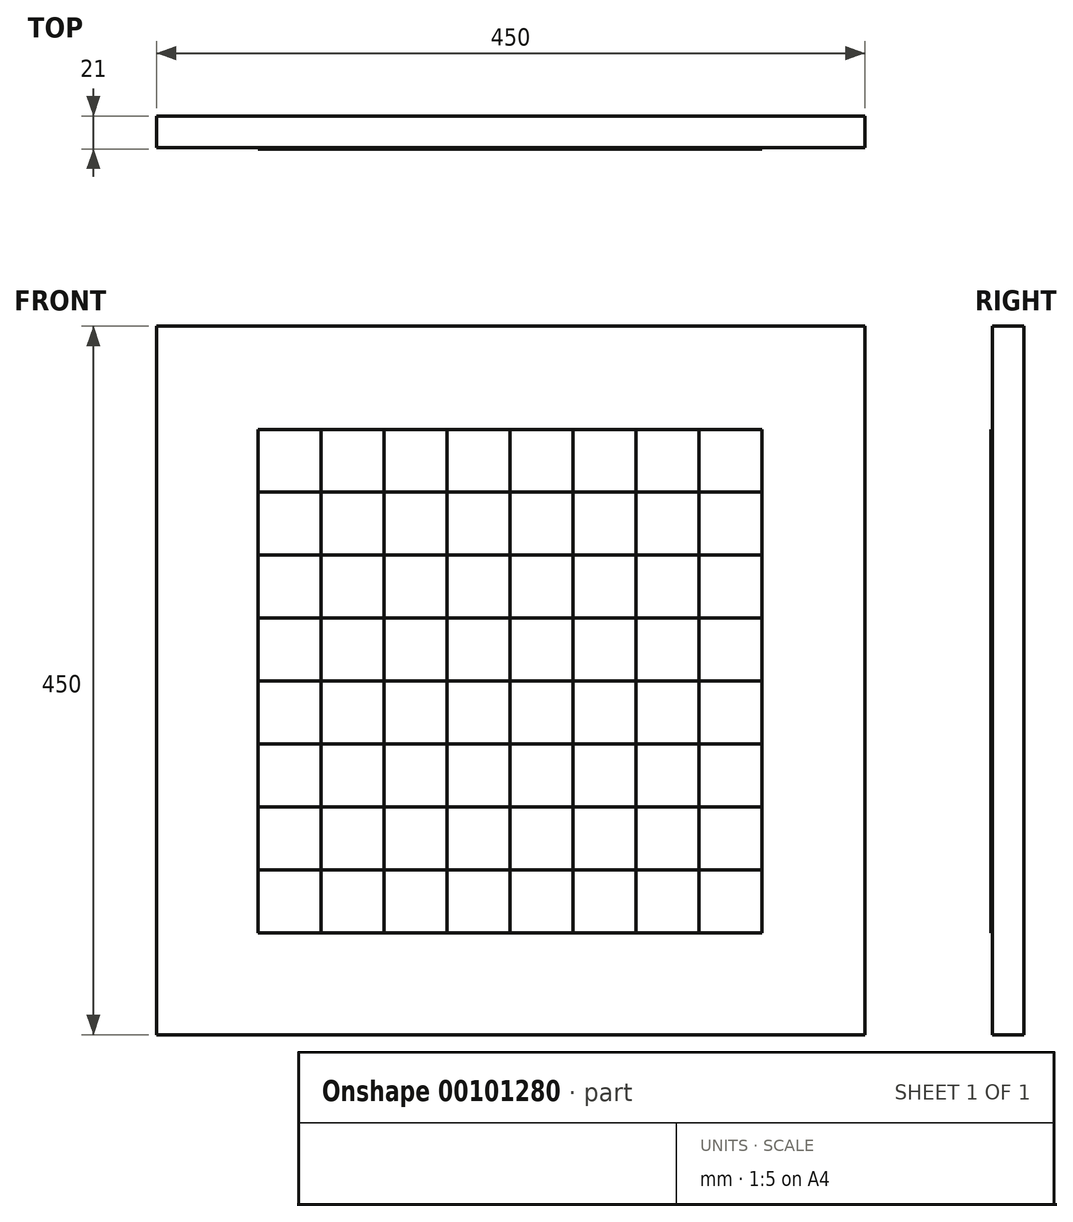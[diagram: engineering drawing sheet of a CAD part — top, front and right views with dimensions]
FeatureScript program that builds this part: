
annotation { "Feature Type Name" : "Feature", "Feature Type Description" : "" }
export const myFeature = defineFeature(function(context is Context, id is Id, definition is map)
    precondition{}
    {
        {
            var Q0;
            Q0=qCreatedBy(makeId("Front.planeOp"),FACE);
            var sketch = newSketch(context, id + "F0", { "sketchPlane" : qUnion([Q0])});
            skLineSegment(sketch, "E0.bottom", {"start": v(0, 0) * mm, "end": v(-450, 0) * mm});
            skLineSegment(sketch, "E0.top", {"start": v(0, 450) * mm, "end": v(-450, 450) * mm});
            skLineSegment(sketch, "E0.left", {"start": v(0, 0) * mm, "end": v(0, 450) * mm});
            skLineSegment(sketch, "E0.right", {"start": v(-450, 0) * mm, "end": v(-450, 450) * mm});
            skSolve(sketch);
        }
        {
            var Q0;
            Q0=makeQuery(id+"F0.imprint","IMPRINT",FACE,{"disambiguationData":[TD([[makeQuery(id+"F0.imprint","IMPRINT",EDGE,{"derivedFrom":sQuery(id+"F0.wireOp",EDGE,"E0.bottom")}),-1.0]])]});
            extrude(context, id + "F1", {"entities" : qUnion([Q0]), "depth" : 20 * mm});
        }
        {
            var Q0;
            Q0=makeQuery(id+"F1.opExtrude","CAP_FACE",FACE,{"disambiguationData":[OSD([sQuery(id+"F0.wireOp",EDGE,"E0.bottom"),sQuery(id+"F0.wireOp",EDGE,"E0.top"),sQuery(id+"F0.wireOp",EDGE,"E0.left"),sQuery(id+"F0.wireOp",EDGE,"E0.right")])],"isStart":false});
            var sketch = newSketch(context, id + "F2", { "sketchPlane" : qUnion([Q0])});
            skLineSegment(sketch, "E1.bottom", {"start": v(-65.47, 64.53) * mm, "end": v(-385.47, 64.53) * mm});
            skLineSegment(sketch, "E1.left", {"start": v(-65.47, 64.53) * mm, "end": v(-65.47, 384.53) * mm});
            skPoint(sketch, "E1.middle", {"position": v(-225.47, 224.53) * mm});
            skLineSegment(sketch, "E2", {"start": v(-65.47, 64.53) * mm, "end": v(0, 0) * mm});
            skLineSegment(sketch, "E3", {"start": v(-385.47, 384.53) * mm, "end": v(-345.47, 384.53) * mm});
            skLineSegment(sketch, "E4", {"start": v(-345.47, 384.53) * mm, "end": v(-305.47, 384.53) * mm});
            skLineSegment(sketch, "E5", {"start": v(-305.47, 384.53) * mm, "end": v(-265.47, 384.53) * mm});
            skLineSegment(sketch, "E6", {"start": v(-265.47, 384.53) * mm, "end": v(-225.47, 384.53) * mm});
            skLineSegment(sketch, "E7", {"start": v(-225.47, 384.53) * mm, "end": v(-185.47, 384.53) * mm});
            skLineSegment(sketch, "E8", {"start": v(-185.47, 384.53) * mm, "end": v(-145.47, 384.53) * mm});
            skLineSegment(sketch, "E9", {"start": v(-145.47, 384.53) * mm, "end": v(-105.47, 384.53) * mm});
            skLineSegment(sketch, "E10", {"start": v(-105.47, 384.53) * mm, "end": v(-65.47, 384.53) * mm});
            skLineSegment(sketch, "E11", {"start": v(-385.47, 384.53) * mm, "end": v(-385.47, 344.53) * mm});
            skLineSegment(sketch, "E12", {"start": v(-385.47, 344.53) * mm, "end": v(-385.47, 304.53) * mm});
            skLineSegment(sketch, "E13", {"start": v(-385.47, 304.53) * mm, "end": v(-385.47, 264.53) * mm});
            skLineSegment(sketch, "E14", {"start": v(-385.47, 264.53) * mm, "end": v(-385.47, 224.53) * mm});
            skLineSegment(sketch, "E15", {"start": v(-385.47, 224.53) * mm, "end": v(-385.47, 184.53) * mm});
            skLineSegment(sketch, "E16", {"start": v(-385.47, 184.53) * mm, "end": v(-385.47, 144.53) * mm});
            skLineSegment(sketch, "E17", {"start": v(-385.47, 144.53) * mm, "end": v(-385.47, 104.53) * mm});
            skLineSegment(sketch, "E18", {"start": v(-385.47, 104.53) * mm, "end": v(-385.47, 64.53) * mm});
            skLineSegment(sketch, "E19", {"start": v(-385.47, 344.53) * mm, "end": v(-65.47, 344.53) * mm});
            skLineSegment(sketch, "E20", {"start": v(-345.47, 384.53) * mm, "end": v(-345.47, 64.53) * mm});
            skLineSegment(sketch, "E21", {"start": v(-385.47, 304.53) * mm, "end": v(-65.47, 304.53) * mm});
            skLineSegment(sketch, "E22", {"start": v(-385.47, 264.53) * mm, "end": v(-65.47, 264.53) * mm});
            skLineSegment(sketch, "E23", {"start": v(-385.47, 224.53) * mm, "end": v(-65.47, 224.53) * mm});
            skLineSegment(sketch, "E24", {"start": v(-385.47, 184.53) * mm, "end": v(-65.47, 184.53) * mm});
            skLineSegment(sketch, "E25", {"start": v(-385.47, 144.53) * mm, "end": v(-65.47, 144.53) * mm});
            skLineSegment(sketch, "E26", {"start": v(-385.47, 104.53) * mm, "end": v(-65.47, 104.53) * mm});
            skLineSegment(sketch, "E27", {"start": v(-305.47, 384.53) * mm, "end": v(-305.47, 64.53) * mm});
            skLineSegment(sketch, "E28", {"start": v(-265.47, 384.53) * mm, "end": v(-265.47, 64.53) * mm});
            skLineSegment(sketch, "E29", {"start": v(-225.47, 384.53) * mm, "end": v(-225.47, 64.53) * mm});
            skLineSegment(sketch, "E30", {"start": v(-185.47, 384.53) * mm, "end": v(-185.47, 64.53) * mm});
            skLineSegment(sketch, "E31", {"start": v(-145.47, 384.53) * mm, "end": v(-145.47, 64.53) * mm});
            skLineSegment(sketch, "E32", {"start": v(-105.47, 384.53) * mm, "end": v(-105.47, 64.53) * mm});
            skLineSegment(sketch, "E33", {"start": v(-450, 450) * mm, "end": v(-385.47, 384.53) * mm});
            skSolve(sketch);
        }
        {
            var Q0;
            Q0=makeQuery(id+"F4.opExtrude","CAP_FACE",FACE,{"disambiguationData":[OSD([sQuery(id+"F2.wireOp",EDGE,"E3"),sQuery(id+"F2.wireOp",EDGE,"E11"),sQuery(id+"F2.wireOp",EDGE,"E19"),sQuery(id+"F2.wireOp",EDGE,"E20")])],"isStart":false});
            var Q1;
            {var subQ0=sQuery(id+"F2.wireOp",EDGE,"E12");Q1=makeQuery(id+"F2.imprint","IMPRINT",FACE,{"disambiguationData":[TD([[makeQuery(id+"F2.imprint","IMPRINT",EDGE,{"derivedFrom":subQ0}),1.0]])]});}
            var Q2;
            {var subQ0=sQuery(id+"F2.wireOp",EDGE,"E4");Q2=makeQuery(id+"F2.imprint","IMPRINT",FACE,{"disambiguationData":[TD([[makeQuery(id+"F2.imprint","IMPRINT",EDGE,{"derivedFrom":subQ0}),-1.0]])]});}
            var Q3;
            {var subQ0=sQuery(id+"F2.wireOp",EDGE,"E27");var subQ1=sQuery(id+"F2.wireOp",EDGE,"E19");var subQ2=makeQuery(id+"F2.imprint","INTERSECT",VERTEX,{"derivedFrom":[subQ1,subQ0]});Q3=makeQuery(id+"F2.imprint","IMPRINT",FACE,{"disambiguationData":[TD([[makeQuery(id+"F2.imprint","IMPRINT",EDGE,{"disambiguationData":[TD([[subQ2,-1.0]])],"derivedFrom":subQ1}),-1.0]])]});}
            var Q4;
            {var subQ0=sQuery(id+"F2.wireOp",EDGE,"E6");Q4=makeQuery(id+"F2.imprint","IMPRINT",FACE,{"disambiguationData":[TD([[makeQuery(id+"F2.imprint","IMPRINT",EDGE,{"derivedFrom":subQ0}),-1.0]])]});}
            var Q5;
            {var subQ0=sQuery(id+"F2.wireOp",EDGE,"E29");var subQ1=sQuery(id+"F2.wireOp",EDGE,"E19");var subQ2=makeQuery(id+"F2.imprint","INTERSECT",VERTEX,{"derivedFrom":[subQ1,subQ0]});Q5=makeQuery(id+"F2.imprint","IMPRINT",FACE,{"disambiguationData":[TD([[makeQuery(id+"F2.imprint","IMPRINT",EDGE,{"disambiguationData":[TD([[subQ2,-1.0]])],"derivedFrom":subQ1}),-1.0]])]});}
            var Q6;
            {var subQ0=sQuery(id+"F2.wireOp",EDGE,"E8");Q6=makeQuery(id+"F2.imprint","IMPRINT",FACE,{"disambiguationData":[TD([[makeQuery(id+"F2.imprint","IMPRINT",EDGE,{"derivedFrom":subQ0}),-1.0]])]});}
            var Q7;
            {var subQ0=sQuery(id+"F2.wireOp",EDGE,"E31");var subQ1=sQuery(id+"F2.wireOp",EDGE,"E19");var subQ2=makeQuery(id+"F2.imprint","INTERSECT",VERTEX,{"derivedFrom":[subQ1,subQ0]});Q7=makeQuery(id+"F2.imprint","IMPRINT",FACE,{"disambiguationData":[TD([[makeQuery(id+"F2.imprint","IMPRINT",EDGE,{"disambiguationData":[TD([[subQ2,-1.0]])],"derivedFrom":subQ1}),-1.0]])]});}
            var Q8;
            {var subQ0=sQuery(id+"F2.wireOp",EDGE,"E10");Q8=makeQuery(id+"F2.imprint","IMPRINT",FACE,{"disambiguationData":[TD([[makeQuery(id+"F2.imprint","IMPRINT",EDGE,{"derivedFrom":subQ0}),-1.0]])]});}
            var Q9;
            {var subQ0=sQuery(id+"F2.wireOp",EDGE,"E21");var subQ1=sQuery(id+"F2.wireOp",EDGE,"E1.left");var subQ2=makeQuery(id+"F2.imprint","INTERSECT",VERTEX,{"derivedFrom":[subQ1,subQ0]});Q9=makeQuery(id+"F2.imprint","IMPRINT",FACE,{"disambiguationData":[TD([[makeQuery(id+"F2.imprint","IMPRINT",EDGE,{"disambiguationData":[TD([[subQ2,1.0]])],"derivedFrom":subQ1}),1.0]])]});}
            var Q10;
            {var subQ0=sQuery(id+"F2.wireOp",EDGE,"E30");var subQ1=sQuery(id+"F2.wireOp",EDGE,"E21");var subQ2=makeQuery(id+"F2.imprint","INTERSECT",VERTEX,{"derivedFrom":[subQ1,subQ0]});Q10=makeQuery(id+"F2.imprint","IMPRINT",FACE,{"disambiguationData":[TD([[makeQuery(id+"F2.imprint","IMPRINT",EDGE,{"disambiguationData":[TD([[subQ2,-1.0]])],"derivedFrom":subQ1}),-1.0]])]});}
            var Q11;
            {var subQ0=sQuery(id+"F2.wireOp",EDGE,"E28");var subQ1=sQuery(id+"F2.wireOp",EDGE,"E21");var subQ2=makeQuery(id+"F2.imprint","INTERSECT",VERTEX,{"derivedFrom":[subQ1,subQ0]});Q11=makeQuery(id+"F2.imprint","IMPRINT",FACE,{"disambiguationData":[TD([[makeQuery(id+"F2.imprint","IMPRINT",EDGE,{"disambiguationData":[TD([[subQ2,-1.0]])],"derivedFrom":subQ1}),-1.0]])]});}
            var Q12;
            {var subQ0=sQuery(id+"F2.wireOp",EDGE,"E21");var subQ1=sQuery(id+"F2.wireOp",EDGE,"E20");var subQ2=makeQuery(id+"F2.imprint","INTERSECT",VERTEX,{"derivedFrom":[subQ1,subQ0]});Q12=makeQuery(id+"F2.imprint","IMPRINT",FACE,{"disambiguationData":[TD([[makeQuery(id+"F2.imprint","IMPRINT",EDGE,{"disambiguationData":[TD([[subQ2,-1.0]])],"derivedFrom":subQ1}),1.0]])]});}
            var Q13;
            {var subQ0=sQuery(id+"F2.wireOp",EDGE,"E14");Q13=makeQuery(id+"F2.imprint","IMPRINT",FACE,{"disambiguationData":[TD([[makeQuery(id+"F2.imprint","IMPRINT",EDGE,{"derivedFrom":subQ0}),1.0]])]});}
            var Q14;
            {var subQ0=sQuery(id+"F2.wireOp",EDGE,"E27");var subQ1=sQuery(id+"F2.wireOp",EDGE,"E22");var subQ2=makeQuery(id+"F2.imprint","INTERSECT",VERTEX,{"derivedFrom":[subQ1,subQ0]});Q14=makeQuery(id+"F2.imprint","IMPRINT",FACE,{"disambiguationData":[TD([[makeQuery(id+"F2.imprint","IMPRINT",EDGE,{"disambiguationData":[TD([[subQ2,-1.0]])],"derivedFrom":subQ1}),-1.0]])]});}
            var Q15;
            {var subQ0=sQuery(id+"F2.wireOp",EDGE,"E29");var subQ1=sQuery(id+"F2.wireOp",EDGE,"E22");var subQ2=makeQuery(id+"F2.imprint","INTERSECT",VERTEX,{"derivedFrom":[subQ1,subQ0]});Q15=makeQuery(id+"F2.imprint","IMPRINT",FACE,{"disambiguationData":[TD([[makeQuery(id+"F2.imprint","IMPRINT",EDGE,{"disambiguationData":[TD([[subQ2,-1.0]])],"derivedFrom":subQ1}),-1.0]])]});}
            var Q16;
            {var subQ0=sQuery(id+"F2.wireOp",EDGE,"E31");var subQ1=sQuery(id+"F2.wireOp",EDGE,"E22");var subQ2=makeQuery(id+"F2.imprint","INTERSECT",VERTEX,{"derivedFrom":[subQ1,subQ0]});Q16=makeQuery(id+"F2.imprint","IMPRINT",FACE,{"disambiguationData":[TD([[makeQuery(id+"F2.imprint","IMPRINT",EDGE,{"disambiguationData":[TD([[subQ2,-1.0]])],"derivedFrom":subQ1}),-1.0]])]});}
            var Q17;
            {var subQ0=sQuery(id+"F2.wireOp",EDGE,"E23");var subQ1=sQuery(id+"F2.wireOp",EDGE,"E1.left");var subQ2=makeQuery(id+"F2.imprint","INTERSECT",VERTEX,{"derivedFrom":[subQ1,subQ0]});Q17=makeQuery(id+"F2.imprint","IMPRINT",FACE,{"disambiguationData":[TD([[makeQuery(id+"F2.imprint","IMPRINT",EDGE,{"disambiguationData":[TD([[subQ2,1.0]])],"derivedFrom":subQ1}),1.0]])]});}
            var Q18;
            {var subQ0=sQuery(id+"F2.wireOp",EDGE,"E30");var subQ1=sQuery(id+"F2.wireOp",EDGE,"E23");var subQ2=makeQuery(id+"F2.imprint","INTERSECT",VERTEX,{"derivedFrom":[subQ1,subQ0]});Q18=makeQuery(id+"F2.imprint","IMPRINT",FACE,{"disambiguationData":[TD([[makeQuery(id+"F2.imprint","IMPRINT",EDGE,{"disambiguationData":[TD([[subQ2,-1.0]])],"derivedFrom":subQ1}),-1.0]])]});}
            var Q19;
            {var subQ0=sQuery(id+"F2.wireOp",EDGE,"E28");var subQ1=sQuery(id+"F2.wireOp",EDGE,"E23");var subQ2=makeQuery(id+"F2.imprint","INTERSECT",VERTEX,{"derivedFrom":[subQ1,subQ0]});Q19=makeQuery(id+"F2.imprint","IMPRINT",FACE,{"disambiguationData":[TD([[makeQuery(id+"F2.imprint","IMPRINT",EDGE,{"disambiguationData":[TD([[subQ2,-1.0]])],"derivedFrom":subQ1}),-1.0]])]});}
            var Q20;
            {var subQ0=sQuery(id+"F2.wireOp",EDGE,"E23");var subQ1=sQuery(id+"F2.wireOp",EDGE,"E20");var subQ2=makeQuery(id+"F2.imprint","INTERSECT",VERTEX,{"derivedFrom":[subQ1,subQ0]});Q20=makeQuery(id+"F2.imprint","IMPRINT",FACE,{"disambiguationData":[TD([[makeQuery(id+"F2.imprint","IMPRINT",EDGE,{"disambiguationData":[TD([[subQ2,-1.0]])],"derivedFrom":subQ1}),1.0]])]});}
            var Q21;
            {var subQ0=sQuery(id+"F2.wireOp",EDGE,"E16");Q21=makeQuery(id+"F2.imprint","IMPRINT",FACE,{"disambiguationData":[TD([[makeQuery(id+"F2.imprint","IMPRINT",EDGE,{"derivedFrom":subQ0}),1.0]])]});}
            var Q22;
            {var subQ0=sQuery(id+"F2.wireOp",EDGE,"E27");var subQ1=sQuery(id+"F2.wireOp",EDGE,"E24");var subQ2=makeQuery(id+"F2.imprint","INTERSECT",VERTEX,{"derivedFrom":[subQ1,subQ0]});Q22=makeQuery(id+"F2.imprint","IMPRINT",FACE,{"disambiguationData":[TD([[makeQuery(id+"F2.imprint","IMPRINT",EDGE,{"disambiguationData":[TD([[subQ2,-1.0]])],"derivedFrom":subQ1}),-1.0]])]});}
            var Q23;
            {var subQ0=sQuery(id+"F2.wireOp",EDGE,"E29");var subQ1=sQuery(id+"F2.wireOp",EDGE,"E24");var subQ2=makeQuery(id+"F2.imprint","INTERSECT",VERTEX,{"derivedFrom":[subQ1,subQ0]});Q23=makeQuery(id+"F2.imprint","IMPRINT",FACE,{"disambiguationData":[TD([[makeQuery(id+"F2.imprint","IMPRINT",EDGE,{"disambiguationData":[TD([[subQ2,-1.0]])],"derivedFrom":subQ1}),-1.0]])]});}
            var Q24;
            {var subQ0=sQuery(id+"F2.wireOp",EDGE,"E31");var subQ1=sQuery(id+"F2.wireOp",EDGE,"E24");var subQ2=makeQuery(id+"F2.imprint","INTERSECT",VERTEX,{"derivedFrom":[subQ1,subQ0]});Q24=makeQuery(id+"F2.imprint","IMPRINT",FACE,{"disambiguationData":[TD([[makeQuery(id+"F2.imprint","IMPRINT",EDGE,{"disambiguationData":[TD([[subQ2,-1.0]])],"derivedFrom":subQ1}),-1.0]])]});}
            var Q25;
            {var subQ0=sQuery(id+"F2.wireOp",EDGE,"E25");var subQ1=sQuery(id+"F2.wireOp",EDGE,"E1.left");var subQ2=makeQuery(id+"F2.imprint","INTERSECT",VERTEX,{"derivedFrom":[subQ1,subQ0]});Q25=makeQuery(id+"F2.imprint","IMPRINT",FACE,{"disambiguationData":[TD([[makeQuery(id+"F2.imprint","IMPRINT",EDGE,{"disambiguationData":[TD([[subQ2,1.0]])],"derivedFrom":subQ1}),1.0]])]});}
            var Q26;
            {var subQ0=sQuery(id+"F2.wireOp",EDGE,"E30");var subQ1=sQuery(id+"F2.wireOp",EDGE,"E25");var subQ2=makeQuery(id+"F2.imprint","INTERSECT",VERTEX,{"derivedFrom":[subQ1,subQ0]});Q26=makeQuery(id+"F2.imprint","IMPRINT",FACE,{"disambiguationData":[TD([[makeQuery(id+"F2.imprint","IMPRINT",EDGE,{"disambiguationData":[TD([[subQ2,-1.0]])],"derivedFrom":subQ1}),-1.0]])]});}
            var Q27;
            {var subQ0=sQuery(id+"F2.wireOp",EDGE,"E28");var subQ1=sQuery(id+"F2.wireOp",EDGE,"E25");var subQ2=makeQuery(id+"F2.imprint","INTERSECT",VERTEX,{"derivedFrom":[subQ1,subQ0]});Q27=makeQuery(id+"F2.imprint","IMPRINT",FACE,{"disambiguationData":[TD([[makeQuery(id+"F2.imprint","IMPRINT",EDGE,{"disambiguationData":[TD([[subQ2,-1.0]])],"derivedFrom":subQ1}),-1.0]])]});}
            var Q28;
            {var subQ0=sQuery(id+"F2.wireOp",EDGE,"E25");var subQ1=sQuery(id+"F2.wireOp",EDGE,"E20");var subQ2=makeQuery(id+"F2.imprint","INTERSECT",VERTEX,{"derivedFrom":[subQ1,subQ0]});Q28=makeQuery(id+"F2.imprint","IMPRINT",FACE,{"disambiguationData":[TD([[makeQuery(id+"F2.imprint","IMPRINT",EDGE,{"disambiguationData":[TD([[subQ2,-1.0]])],"derivedFrom":subQ1}),1.0]])]});}
            var Q29;
            {var subQ0=sQuery(id+"F2.wireOp",EDGE,"E18");Q29=makeQuery(id+"F2.imprint","IMPRINT",FACE,{"disambiguationData":[TD([[makeQuery(id+"F2.imprint","IMPRINT",EDGE,{"derivedFrom":subQ0}),1.0]])]});}
            var Q30;
            {var subQ0=sQuery(id+"F2.wireOp",EDGE,"E27");var subQ1=sQuery(id+"F2.wireOp",EDGE,"E1.bottom");var subQ2=makeQuery(id+"F2.imprint","INTERSECT",VERTEX,{"derivedFrom":[subQ1,subQ0]});Q30=makeQuery(id+"F2.imprint","IMPRINT",FACE,{"disambiguationData":[TD([[makeQuery(id+"F2.imprint","IMPRINT",EDGE,{"disambiguationData":[TD([[subQ2,1.0]])],"derivedFrom":subQ1}),-1.0]])]});}
            var Q31;
            {var subQ0=sQuery(id+"F2.wireOp",EDGE,"E29");var subQ1=sQuery(id+"F2.wireOp",EDGE,"E1.bottom");var subQ2=makeQuery(id+"F2.imprint","INTERSECT",VERTEX,{"derivedFrom":[subQ1,subQ0]});Q31=makeQuery(id+"F2.imprint","IMPRINT",FACE,{"disambiguationData":[TD([[makeQuery(id+"F2.imprint","IMPRINT",EDGE,{"disambiguationData":[TD([[subQ2,1.0]])],"derivedFrom":subQ1}),-1.0]])]});}
            var Q32;
            {var subQ0=sQuery(id+"F2.wireOp",EDGE,"E31");var subQ1=sQuery(id+"F2.wireOp",EDGE,"E1.bottom");var subQ2=makeQuery(id+"F2.imprint","INTERSECT",VERTEX,{"derivedFrom":[subQ1,subQ0]});Q32=makeQuery(id+"F2.imprint","IMPRINT",FACE,{"disambiguationData":[TD([[makeQuery(id+"F2.imprint","IMPRINT",EDGE,{"disambiguationData":[TD([[subQ2,1.0]])],"derivedFrom":subQ1}),-1.0]])]});}
            extrude(context, id + "F3", {"entities" : qUnion([Q0, Q1, Q2, Q3, Q4, Q5, Q6, Q7, Q8, Q9, Q10, Q11, Q12, Q13, Q14, Q15, Q16, Q17, Q18, Q19, Q20, Q21, Q22, Q23, Q24, Q25, Q26, Q27, Q28, Q29, Q30, Q31, Q32]), "depth" : 1 * mm});
        }
        {
            var Q0;
            {var subQ0=sQuery(id+"F2.wireOp",EDGE,"E3");Q0=makeQuery(id+"F2.imprint","IMPRINT",FACE,{"disambiguationData":[TD([[makeQuery(id+"F2.imprint","IMPRINT",EDGE,{"derivedFrom":subQ0}),-1.0]])]});}
            var Q1;
            {var subQ0=sQuery(id+"F2.wireOp",EDGE,"E20");var subQ1=sQuery(id+"F2.wireOp",EDGE,"E19");var subQ2=makeQuery(id+"F2.imprint","INTERSECT",VERTEX,{"derivedFrom":[subQ1,subQ0]});Q1=makeQuery(id+"F2.imprint","IMPRINT",FACE,{"disambiguationData":[TD([[makeQuery(id+"F2.imprint","IMPRINT",EDGE,{"disambiguationData":[TD([[subQ2,-1.0]])],"derivedFrom":subQ1}),-1.0]])]});}
            var Q2;
            {var subQ0=sQuery(id+"F2.wireOp",EDGE,"E5");Q2=makeQuery(id+"F2.imprint","IMPRINT",FACE,{"disambiguationData":[TD([[makeQuery(id+"F2.imprint","IMPRINT",EDGE,{"derivedFrom":subQ0}),-1.0]])]});}
            var Q3;
            {var subQ0=sQuery(id+"F2.wireOp",EDGE,"E13");Q3=makeQuery(id+"F2.imprint","IMPRINT",FACE,{"disambiguationData":[TD([[makeQuery(id+"F2.imprint","IMPRINT",EDGE,{"derivedFrom":subQ0}),1.0]])]});}
            var Q4;
            {var subQ0=sQuery(id+"F2.wireOp",EDGE,"E27");var subQ1=sQuery(id+"F2.wireOp",EDGE,"E21");var subQ2=makeQuery(id+"F2.imprint","INTERSECT",VERTEX,{"derivedFrom":[subQ1,subQ0]});Q4=makeQuery(id+"F2.imprint","IMPRINT",FACE,{"disambiguationData":[TD([[makeQuery(id+"F2.imprint","IMPRINT",EDGE,{"disambiguationData":[TD([[subQ2,-1.0]])],"derivedFrom":subQ1}),-1.0]])]});}
            var Q5;
            {var subQ0=sQuery(id+"F2.wireOp",EDGE,"E28");var subQ1=sQuery(id+"F2.wireOp",EDGE,"E19");var subQ2=makeQuery(id+"F2.imprint","INTERSECT",VERTEX,{"derivedFrom":[subQ1,subQ0]});Q5=makeQuery(id+"F2.imprint","IMPRINT",FACE,{"disambiguationData":[TD([[makeQuery(id+"F2.imprint","IMPRINT",EDGE,{"disambiguationData":[TD([[subQ2,-1.0]])],"derivedFrom":subQ1}),-1.0]])]});}
            var Q6;
            {var subQ0=sQuery(id+"F2.wireOp",EDGE,"E7");Q6=makeQuery(id+"F2.imprint","IMPRINT",FACE,{"disambiguationData":[TD([[makeQuery(id+"F2.imprint","IMPRINT",EDGE,{"derivedFrom":subQ0}),-1.0]])]});}
            var Q7;
            {var subQ0=sQuery(id+"F2.wireOp",EDGE,"E29");var subQ1=sQuery(id+"F2.wireOp",EDGE,"E21");var subQ2=makeQuery(id+"F2.imprint","INTERSECT",VERTEX,{"derivedFrom":[subQ1,subQ0]});Q7=makeQuery(id+"F2.imprint","IMPRINT",FACE,{"disambiguationData":[TD([[makeQuery(id+"F2.imprint","IMPRINT",EDGE,{"disambiguationData":[TD([[subQ2,-1.0]])],"derivedFrom":subQ1}),-1.0]])]});}
            var Q8;
            {var subQ0=sQuery(id+"F2.wireOp",EDGE,"E30");var subQ1=sQuery(id+"F2.wireOp",EDGE,"E19");var subQ2=makeQuery(id+"F2.imprint","INTERSECT",VERTEX,{"derivedFrom":[subQ1,subQ0]});Q8=makeQuery(id+"F2.imprint","IMPRINT",FACE,{"disambiguationData":[TD([[makeQuery(id+"F2.imprint","IMPRINT",EDGE,{"disambiguationData":[TD([[subQ2,-1.0]])],"derivedFrom":subQ1}),-1.0]])]});}
            var Q9;
            {var subQ0=sQuery(id+"F2.wireOp",EDGE,"E9");Q9=makeQuery(id+"F2.imprint","IMPRINT",FACE,{"disambiguationData":[TD([[makeQuery(id+"F2.imprint","IMPRINT",EDGE,{"derivedFrom":subQ0}),-1.0]])]});}
            var Q10;
            {var subQ0=sQuery(id+"F2.wireOp",EDGE,"E31");var subQ1=sQuery(id+"F2.wireOp",EDGE,"E21");var subQ2=makeQuery(id+"F2.imprint","INTERSECT",VERTEX,{"derivedFrom":[subQ1,subQ0]});Q10=makeQuery(id+"F2.imprint","IMPRINT",FACE,{"disambiguationData":[TD([[makeQuery(id+"F2.imprint","IMPRINT",EDGE,{"disambiguationData":[TD([[subQ2,-1.0]])],"derivedFrom":subQ1}),-1.0]])]});}
            var Q11;
            {var subQ0=sQuery(id+"F2.wireOp",EDGE,"E19");var subQ1=sQuery(id+"F2.wireOp",EDGE,"E1.left");var subQ2=makeQuery(id+"F2.imprint","INTERSECT",VERTEX,{"derivedFrom":[subQ1,subQ0]});Q11=makeQuery(id+"F2.imprint","IMPRINT",FACE,{"disambiguationData":[TD([[makeQuery(id+"F2.imprint","IMPRINT",EDGE,{"disambiguationData":[TD([[subQ2,1.0]])],"derivedFrom":subQ1}),1.0]])]});}
            var Q12;
            {var subQ0=sQuery(id+"F2.wireOp",EDGE,"E22");var subQ1=sQuery(id+"F2.wireOp",EDGE,"E1.left");var subQ2=makeQuery(id+"F2.imprint","INTERSECT",VERTEX,{"derivedFrom":[subQ1,subQ0]});Q12=makeQuery(id+"F2.imprint","IMPRINT",FACE,{"disambiguationData":[TD([[makeQuery(id+"F2.imprint","IMPRINT",EDGE,{"disambiguationData":[TD([[subQ2,1.0]])],"derivedFrom":subQ1}),1.0]])]});}
            var Q13;
            {var subQ0=sQuery(id+"F2.wireOp",EDGE,"E30");var subQ1=sQuery(id+"F2.wireOp",EDGE,"E22");var subQ2=makeQuery(id+"F2.imprint","INTERSECT",VERTEX,{"derivedFrom":[subQ1,subQ0]});Q13=makeQuery(id+"F2.imprint","IMPRINT",FACE,{"disambiguationData":[TD([[makeQuery(id+"F2.imprint","IMPRINT",EDGE,{"disambiguationData":[TD([[subQ2,-1.0]])],"derivedFrom":subQ1}),-1.0]])]});}
            var Q14;
            {var subQ0=sQuery(id+"F2.wireOp",EDGE,"E28");var subQ1=sQuery(id+"F2.wireOp",EDGE,"E22");var subQ2=makeQuery(id+"F2.imprint","INTERSECT",VERTEX,{"derivedFrom":[subQ1,subQ0]});Q14=makeQuery(id+"F2.imprint","IMPRINT",FACE,{"disambiguationData":[TD([[makeQuery(id+"F2.imprint","IMPRINT",EDGE,{"disambiguationData":[TD([[subQ2,-1.0]])],"derivedFrom":subQ1}),-1.0]])]});}
            var Q15;
            {var subQ0=sQuery(id+"F2.wireOp",EDGE,"E22");var subQ1=sQuery(id+"F2.wireOp",EDGE,"E20");var subQ2=makeQuery(id+"F2.imprint","INTERSECT",VERTEX,{"derivedFrom":[subQ1,subQ0]});Q15=makeQuery(id+"F2.imprint","IMPRINT",FACE,{"disambiguationData":[TD([[makeQuery(id+"F2.imprint","IMPRINT",EDGE,{"disambiguationData":[TD([[subQ2,-1.0]])],"derivedFrom":subQ1}),1.0]])]});}
            var Q16;
            {var subQ0=sQuery(id+"F2.wireOp",EDGE,"E15");Q16=makeQuery(id+"F2.imprint","IMPRINT",FACE,{"disambiguationData":[TD([[makeQuery(id+"F2.imprint","IMPRINT",EDGE,{"derivedFrom":subQ0}),1.0]])]});}
            var Q17;
            {var subQ0=sQuery(id+"F2.wireOp",EDGE,"E27");var subQ1=sQuery(id+"F2.wireOp",EDGE,"E23");var subQ2=makeQuery(id+"F2.imprint","INTERSECT",VERTEX,{"derivedFrom":[subQ1,subQ0]});Q17=makeQuery(id+"F2.imprint","IMPRINT",FACE,{"disambiguationData":[TD([[makeQuery(id+"F2.imprint","IMPRINT",EDGE,{"disambiguationData":[TD([[subQ2,-1.0]])],"derivedFrom":subQ1}),-1.0]])]});}
            var Q18;
            {var subQ0=sQuery(id+"F2.wireOp",EDGE,"E29");var subQ1=sQuery(id+"F2.wireOp",EDGE,"E23");var subQ2=makeQuery(id+"F2.imprint","INTERSECT",VERTEX,{"derivedFrom":[subQ1,subQ0]});Q18=makeQuery(id+"F2.imprint","IMPRINT",FACE,{"disambiguationData":[TD([[makeQuery(id+"F2.imprint","IMPRINT",EDGE,{"disambiguationData":[TD([[subQ2,-1.0]])],"derivedFrom":subQ1}),-1.0]])]});}
            var Q19;
            {var subQ0=sQuery(id+"F2.wireOp",EDGE,"E31");var subQ1=sQuery(id+"F2.wireOp",EDGE,"E23");var subQ2=makeQuery(id+"F2.imprint","INTERSECT",VERTEX,{"derivedFrom":[subQ1,subQ0]});Q19=makeQuery(id+"F2.imprint","IMPRINT",FACE,{"disambiguationData":[TD([[makeQuery(id+"F2.imprint","IMPRINT",EDGE,{"disambiguationData":[TD([[subQ2,-1.0]])],"derivedFrom":subQ1}),-1.0]])]});}
            var Q20;
            {var subQ0=sQuery(id+"F2.wireOp",EDGE,"E24");var subQ1=sQuery(id+"F2.wireOp",EDGE,"E1.left");var subQ2=makeQuery(id+"F2.imprint","INTERSECT",VERTEX,{"derivedFrom":[subQ1,subQ0]});Q20=makeQuery(id+"F2.imprint","IMPRINT",FACE,{"disambiguationData":[TD([[makeQuery(id+"F2.imprint","IMPRINT",EDGE,{"disambiguationData":[TD([[subQ2,1.0]])],"derivedFrom":subQ1}),1.0]])]});}
            var Q21;
            {var subQ0=sQuery(id+"F2.wireOp",EDGE,"E30");var subQ1=sQuery(id+"F2.wireOp",EDGE,"E24");var subQ2=makeQuery(id+"F2.imprint","INTERSECT",VERTEX,{"derivedFrom":[subQ1,subQ0]});Q21=makeQuery(id+"F2.imprint","IMPRINT",FACE,{"disambiguationData":[TD([[makeQuery(id+"F2.imprint","IMPRINT",EDGE,{"disambiguationData":[TD([[subQ2,-1.0]])],"derivedFrom":subQ1}),-1.0]])]});}
            var Q22;
            {var subQ0=sQuery(id+"F2.wireOp",EDGE,"E28");var subQ1=sQuery(id+"F2.wireOp",EDGE,"E24");var subQ2=makeQuery(id+"F2.imprint","INTERSECT",VERTEX,{"derivedFrom":[subQ1,subQ0]});Q22=makeQuery(id+"F2.imprint","IMPRINT",FACE,{"disambiguationData":[TD([[makeQuery(id+"F2.imprint","IMPRINT",EDGE,{"disambiguationData":[TD([[subQ2,-1.0]])],"derivedFrom":subQ1}),-1.0]])]});}
            var Q23;
            {var subQ0=sQuery(id+"F2.wireOp",EDGE,"E24");var subQ1=sQuery(id+"F2.wireOp",EDGE,"E20");var subQ2=makeQuery(id+"F2.imprint","INTERSECT",VERTEX,{"derivedFrom":[subQ1,subQ0]});Q23=makeQuery(id+"F2.imprint","IMPRINT",FACE,{"disambiguationData":[TD([[makeQuery(id+"F2.imprint","IMPRINT",EDGE,{"disambiguationData":[TD([[subQ2,-1.0]])],"derivedFrom":subQ1}),1.0]])]});}
            var Q24;
            {var subQ0=sQuery(id+"F2.wireOp",EDGE,"E17");Q24=makeQuery(id+"F2.imprint","IMPRINT",FACE,{"disambiguationData":[TD([[makeQuery(id+"F2.imprint","IMPRINT",EDGE,{"derivedFrom":subQ0}),1.0]])]});}
            var Q25;
            {var subQ0=sQuery(id+"F2.wireOp",EDGE,"E27");var subQ1=sQuery(id+"F2.wireOp",EDGE,"E25");var subQ2=makeQuery(id+"F2.imprint","INTERSECT",VERTEX,{"derivedFrom":[subQ1,subQ0]});Q25=makeQuery(id+"F2.imprint","IMPRINT",FACE,{"disambiguationData":[TD([[makeQuery(id+"F2.imprint","IMPRINT",EDGE,{"disambiguationData":[TD([[subQ2,-1.0]])],"derivedFrom":subQ1}),-1.0]])]});}
            var Q26;
            {var subQ0=sQuery(id+"F2.wireOp",EDGE,"E29");var subQ1=sQuery(id+"F2.wireOp",EDGE,"E25");var subQ2=makeQuery(id+"F2.imprint","INTERSECT",VERTEX,{"derivedFrom":[subQ1,subQ0]});Q26=makeQuery(id+"F2.imprint","IMPRINT",FACE,{"disambiguationData":[TD([[makeQuery(id+"F2.imprint","IMPRINT",EDGE,{"disambiguationData":[TD([[subQ2,-1.0]])],"derivedFrom":subQ1}),-1.0]])]});}
            var Q27;
            {var subQ0=sQuery(id+"F2.wireOp",EDGE,"E31");var subQ1=sQuery(id+"F2.wireOp",EDGE,"E25");var subQ2=makeQuery(id+"F2.imprint","INTERSECT",VERTEX,{"derivedFrom":[subQ1,subQ0]});Q27=makeQuery(id+"F2.imprint","IMPRINT",FACE,{"disambiguationData":[TD([[makeQuery(id+"F2.imprint","IMPRINT",EDGE,{"disambiguationData":[TD([[subQ2,-1.0]])],"derivedFrom":subQ1}),-1.0]])]});}
            var Q28;
            {var subQ0=sQuery(id+"F2.wireOp",EDGE,"E1.left");var subQ5=sQuery(id+"F2.wireOp",EDGE,"E26");var subQ6=makeQuery(id+"F2.imprint","INTERSECT",VERTEX,{"derivedFrom":[subQ0,subQ5]});Q28=makeQuery(id+"F2.imprint","IMPRINT",FACE,{"disambiguationData":[TD([[makeQuery(id+"F2.imprint","IMPRINT",EDGE,{"disambiguationData":[TD([[subQ6,1.0]])],"derivedFrom":subQ5}),-1.0]])]});}
            var Q29;
            {var subQ0=sQuery(id+"F2.wireOp",EDGE,"E30");var subQ1=sQuery(id+"F2.wireOp",EDGE,"E1.bottom");var subQ2=makeQuery(id+"F2.imprint","INTERSECT",VERTEX,{"derivedFrom":[subQ1,subQ0]});Q29=makeQuery(id+"F2.imprint","IMPRINT",FACE,{"disambiguationData":[TD([[makeQuery(id+"F2.imprint","IMPRINT",EDGE,{"disambiguationData":[TD([[subQ2,1.0]])],"derivedFrom":subQ1}),-1.0]])]});}
            var Q30;
            {var subQ0=sQuery(id+"F2.wireOp",EDGE,"E28");var subQ1=sQuery(id+"F2.wireOp",EDGE,"E1.bottom");var subQ2=makeQuery(id+"F2.imprint","INTERSECT",VERTEX,{"derivedFrom":[subQ1,subQ0]});Q30=makeQuery(id+"F2.imprint","IMPRINT",FACE,{"disambiguationData":[TD([[makeQuery(id+"F2.imprint","IMPRINT",EDGE,{"disambiguationData":[TD([[subQ2,1.0]])],"derivedFrom":subQ1}),-1.0]])]});}
            var Q31;
            {var subQ0=sQuery(id+"F2.wireOp",EDGE,"E20");var subQ1=sQuery(id+"F2.wireOp",EDGE,"E1.bottom");var subQ2=makeQuery(id+"F2.imprint","INTERSECT",VERTEX,{"derivedFrom":[subQ1,subQ0]});Q31=makeQuery(id+"F2.imprint","IMPRINT",FACE,{"disambiguationData":[TD([[makeQuery(id+"F2.imprint","IMPRINT",EDGE,{"disambiguationData":[TD([[subQ2,1.0]])],"derivedFrom":subQ1}),-1.0]])]});}
            extrude(context, id + "F4", {"entities" : qUnion([Q0, Q1, Q2, Q3, Q4, Q5, Q6, Q7, Q8, Q9, Q10, Q11, Q12, Q13, Q14, Q15, Q16, Q17, Q18, Q19, Q20, Q21, Q22, Q23, Q24, Q25, Q26, Q27, Q28, Q29, Q30, Q31]), "depth" : 1 * mm});
        }
    });
